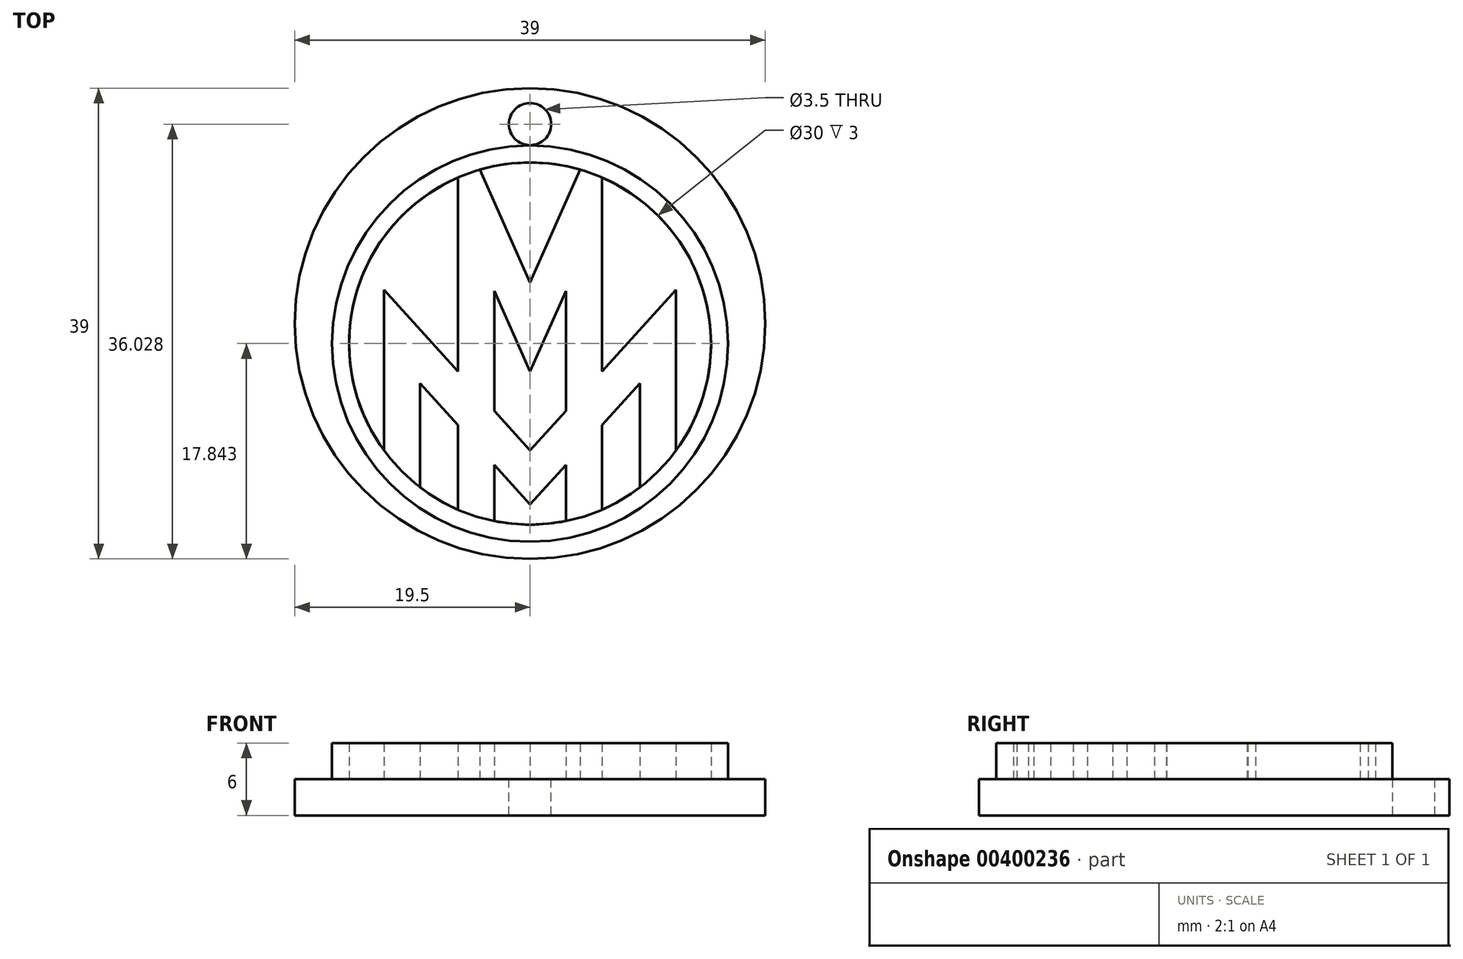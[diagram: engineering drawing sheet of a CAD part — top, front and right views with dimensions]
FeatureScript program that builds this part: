
annotation { "Feature Type Name" : "Feature", "Feature Type Description" : "" }
export const myFeature = defineFeature(function(context is Context, id is Id, definition is map)
    precondition{}
    {
        {
            var Q0;
            Q0=qCreatedBy(makeId("Top.planeOp"),FACE);
            var sketch = newSketch(context, id + "F0", { "sketchPlane" : qUnion([Q0])});
            skCircle(sketch, "E0", {"center": v(0, -1.66) * mm, "radius": 15 * mm});
            skLineSegment(sketch, "E1", {"start": v(-5.97, -15.42) * mm, "end": v(-5.97, -8.4) * mm});
            skLineSegment(sketch, "E2", {"start": v(-4.15, 12.76) * mm, "end": v(0, 3.41) * mm});
            skLineSegment(sketch, "E3.MirrorCS", {"start": v(4.15, 12.76) * mm, "end": v(0, 3.41) * mm});
            skLineSegment(sketch, "E4.MirrorCS", {"start": v(5.97, -15.42) * mm, "end": v(5.97, -8.4) * mm});
            skLineSegment(sketch, "E5", {"start": v(-12.1, -10.52) * mm, "end": v(-12.1, 2.8) * mm});
            skLineSegment(sketch, "E6", {"start": v(-12.1, 2.8) * mm, "end": v(-5.97, -3.95) * mm});
            skLineSegment(sketch, "E7.MirrorCS", {"start": v(12.1, -10.52) * mm, "end": v(12.1, 2.8) * mm});
            skLineSegment(sketch, "E8.MirrorCS", {"start": v(12.1, 2.8) * mm, "end": v(5.97, -3.95) * mm});
            skLineSegment(sketch, "E9.0", {"start": v(9.1, -13.58) * mm, "end": v(9.1, -4.96) * mm});
            skLineSegment(sketch, "E9.1", {"start": v(9.1, -4.96) * mm, "end": v(5.97, -8.4) * mm});
            skLineSegment(sketch, "E9.2", {"start": v(-9.1, -4.96) * mm, "end": v(-5.97, -8.4) * mm});
            skLineSegment(sketch, "E9.3", {"start": v(-9.1, -13.58) * mm, "end": v(-9.1, -4.96) * mm});
            skLineSegment(sketch, "E10.0", {"start": v(2.97, -13.73) * mm, "end": v(2.97, -11.7) * mm});
            skLineSegment(sketch, "E10.1", {"start": v(2.97, 2.71) * mm, "end": v(0, -3.98) * mm});
            skLineSegment(sketch, "E10.2", {"start": v(-2.97, 2.71) * mm, "end": v(0, -3.98) * mm});
            skLineSegment(sketch, "E10.3", {"start": v(-2.97, -16.36) * mm, "end": v(-2.97, -11.7) * mm});
            skLineSegment(sketch, "E11.trimOffspring", {"start": v(-2.97, -7.25) * mm, "end": v(-2.97, 2.71) * mm});
            skLineSegment(sketch, "E12.trimOffspring", {"start": v(-5.97, -3.95) * mm, "end": v(-5.97, 12.1) * mm});
            skLineSegment(sketch, "E13.trimOffspring", {"start": v(2.97, -7.25) * mm, "end": v(2.97, 2.71) * mm});
            skLineSegment(sketch, "E14.trimOffspring", {"start": v(5.97, -3.95) * mm, "end": v(5.97, 12.1) * mm});
            skLineSegment(sketch, "E15.trimOffspring", {"start": v(2.97, -7.25) * mm, "end": v(0, -10.52) * mm});
            skLineSegment(sketch, "E16.trimOffspring", {"start": v(-2.97, -7.25) * mm, "end": v(0, -10.52) * mm});
            skLineSegment(sketch, "E17.trimOffspring", {"start": v(2.97, -11.7) * mm, "end": v(0, -14.98) * mm});
            skLineSegment(sketch, "E18.trimOffspring", {"start": v(-2.97, -11.7) * mm, "end": v(0, -14.98) * mm});
            skLineSegment(sketch, "E19", {"start": v(2.97, -13.73) * mm, "end": v(2.97, -16.36) * mm});
            skPoint(sketch, "E20.orphan", {"position": v(-6.1, 17.13) * mm});
            skPoint(sketch, "E21.orphan", {"position": v(-5.97, 13.73) * mm});
            skPoint(sketch, "E22.orphan", {"position": v(6.1, 17.13) * mm});
            skPoint(sketch, "E23.orphan", {"position": v(5.97, 13.73) * mm});
            skCircle(sketch, "E24", {"center": v(0, -1.66) * mm, "radius": 16.41 * mm});
            skSolve(sketch);
        }
        {
            var Q0;
            {var subQ0=sQuery(id+"F0.wireOp",EDGE,"E5");Q0=makeQuery(id+"F0.imprint","IMPRINT",FACE,{"disambiguationData":[TD([[makeQuery(id+"F0.imprint","IMPRINT",EDGE,{"derivedFrom":subQ0}),1.0]])]});}
            var Q1;
            {var subQ0=sQuery(id+"F0.wireOp",EDGE,"E2");Q1=makeQuery(id+"F0.imprint","IMPRINT",FACE,{"disambiguationData":[TD([[makeQuery(id+"F0.imprint","IMPRINT",EDGE,{"derivedFrom":subQ0}),1.0]])]});}
            var Q2;
            {var subQ0=sQuery(id+"F0.wireOp",EDGE,"E7.MirrorCS");Q2=makeQuery(id+"F0.imprint","IMPRINT",FACE,{"disambiguationData":[TD([[makeQuery(id+"F0.imprint","IMPRINT",EDGE,{"derivedFrom":subQ0}),-1.0]])]});}
            var Q3;
            {var subQ0=sQuery(id+"F0.wireOp",EDGE,"E4.MirrorCS");Q3=makeQuery(id+"F0.imprint","IMPRINT",FACE,{"disambiguationData":[TD([[makeQuery(id+"F0.imprint","IMPRINT",EDGE,{"derivedFrom":subQ0}),-1.0]])]});}
            var Q4;
            Q4=makeQuery(id+"F0.imprint","IMPRINT",FACE,{"disambiguationData":[TD([[makeQuery(id+"F0.imprint","IMPRINT",EDGE,{"derivedFrom":sQuery(id+"F0.wireOp",EDGE,"E10.1")}),1.0]])]});
            var Q5;
            Q5=makeQuery(id+"F0.imprint","IMPRINT",FACE,{"disambiguationData":[TD([[makeQuery(id+"F0.imprint","IMPRINT",EDGE,{"derivedFrom":sQuery(id+"F0.wireOp",EDGE,"E10.0")}),1.0]])]});
            var Q6;
            {var subQ0=sQuery(id+"F0.wireOp",EDGE,"E1");Q6=makeQuery(id+"F0.imprint","IMPRINT",FACE,{"disambiguationData":[TD([[makeQuery(id+"F0.imprint","IMPRINT",EDGE,{"derivedFrom":subQ0}),1.0]])]});}
            extrude(context, id + "F1", {"entities" : qUnion([Q0, Q1, Q2, Q3, Q4, Q5, Q6]), "depth" : 3 * mm});
        }
        {
            var Q0;
            Q0=qCreatedBy(makeId("Top.planeOp"),FACE);
            var sketch = newSketch(context, id + "F2", { "sketchPlane" : qUnion([Q0])});
            skCircle(sketch, "E25", {"center": v(0, 0) * mm, "radius": 19.5 * mm});
            skCircle(sketch, "E26", {"center": v(0, 16.53) * mm, "radius": 1.75 * mm});
            skSolve(sketch);
        }
        {
            var Q0;
            Q0=makeQuery(id+"F2.imprint","IMPRINT",FACE,{"disambiguationData":[TD([[makeQuery(id+"F2.imprint","IMPRINT",EDGE,{"derivedFrom":sQuery(id+"F2.wireOp",EDGE,"E25")}),1.0]])]});
            extrude(context, id + "F3", {"entities" : qUnion([Q0]), "oppositeDirection" : true, "depth" : 3 * mm});
        }
        {
            var Q0;
            Q0=makeQuery(id+"F0.imprint","IMPRINT",FACE,{"disambiguationData":[TD([[makeQuery(id+"F0.imprint","IMPRINT",EDGE,{"derivedFrom":sQuery(id+"F0.wireOp",EDGE,"E24")}),1.0]])]});
            extrude(context, id + "F4", {"entities" : qUnion([Q0]), "depth" : 3 * mm});
        }
    });
